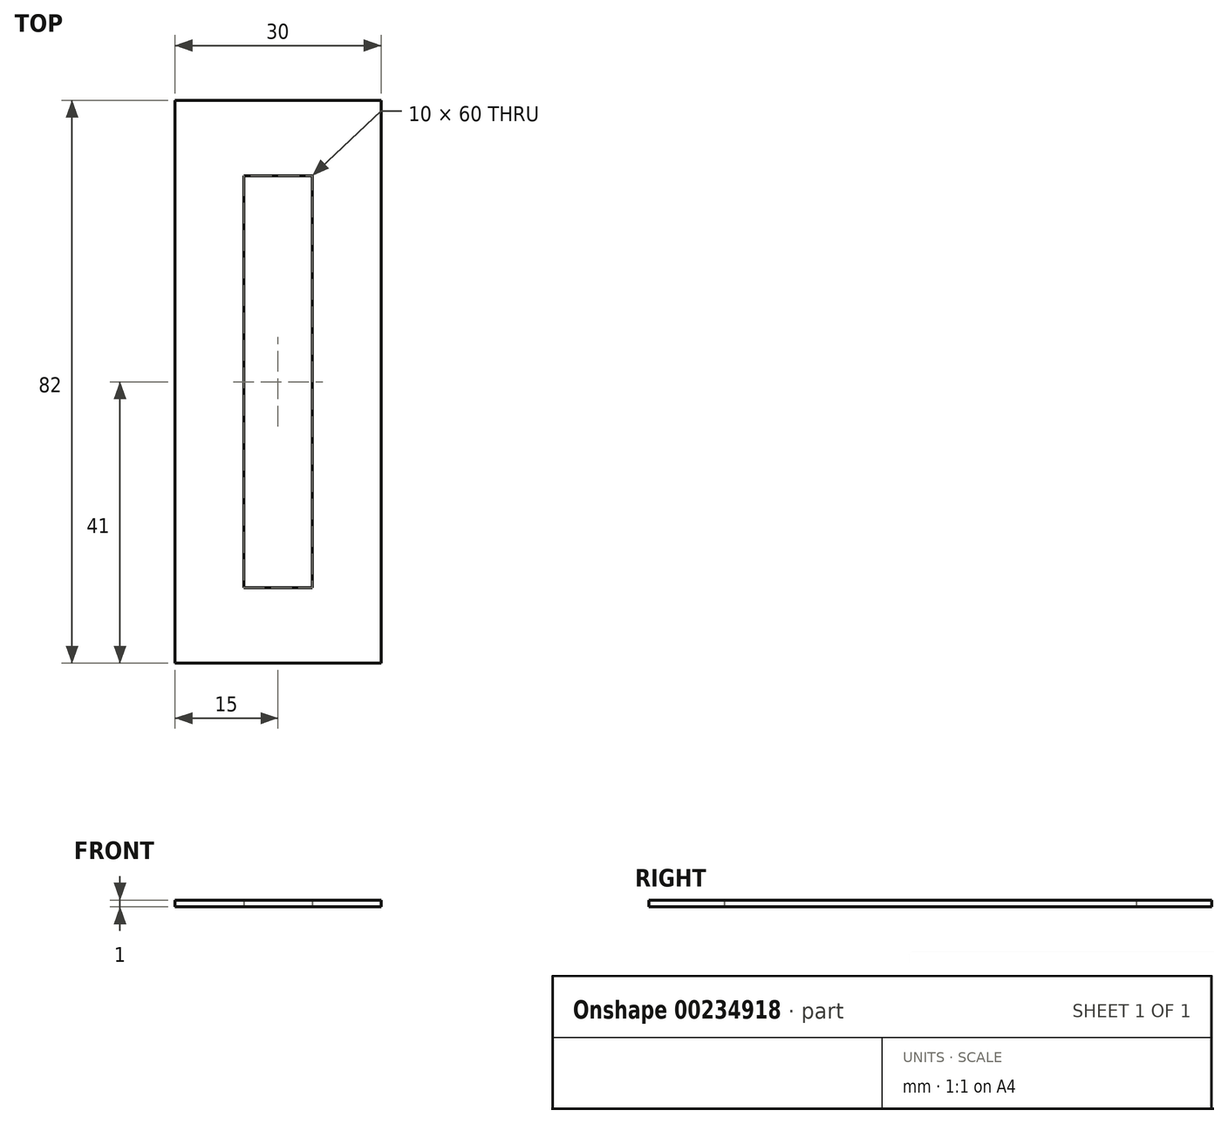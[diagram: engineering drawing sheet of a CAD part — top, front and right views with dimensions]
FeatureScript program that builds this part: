
annotation { "Feature Type Name" : "Feature", "Feature Type Description" : "" }
export const myFeature = defineFeature(function(context is Context, id is Id, definition is map)
    precondition{}
    {
        {
            var Q0;
            Q0=qCreatedBy(makeId("Top.planeOp"),FACE);
            var sketch = newSketch(context, id + "F0", { "sketchPlane" : qUnion([Q0])});
            skLineSegment(sketch, "E0.bottom", {"start": v(5, 30) * mm, "end": v(-5, 30) * mm});
            skLineSegment(sketch, "E0.top", {"start": v(5, -30) * mm, "end": v(-5, -30) * mm});
            skLineSegment(sketch, "E0.left", {"start": v(5, 30) * mm, "end": v(5, -30) * mm});
            skLineSegment(sketch, "E0.right", {"start": v(-5, 30) * mm, "end": v(-5, -30) * mm});
            skPoint(sketch, "E0.middle", {"position": v(0, 0) * mm});
            skLineSegment(sketch, "E1.bottom", {"start": v(15, 41) * mm, "end": v(-15, 41) * mm});
            skLineSegment(sketch, "E1.top", {"start": v(15, -41) * mm, "end": v(-15, -41) * mm});
            skLineSegment(sketch, "E1.left", {"start": v(15, 41) * mm, "end": v(15, -41) * mm});
            skLineSegment(sketch, "E1.right", {"start": v(-15, 41) * mm, "end": v(-15, -41) * mm});
            skSolve(sketch);
        }
        {
            var Q0;
            Q0 = qSketchRegion(id + "F0", true);
            extrude(context, id + "F1", {"entities" : qUnion([Q0]), "depth" : 1 * mm});
        }
    });
